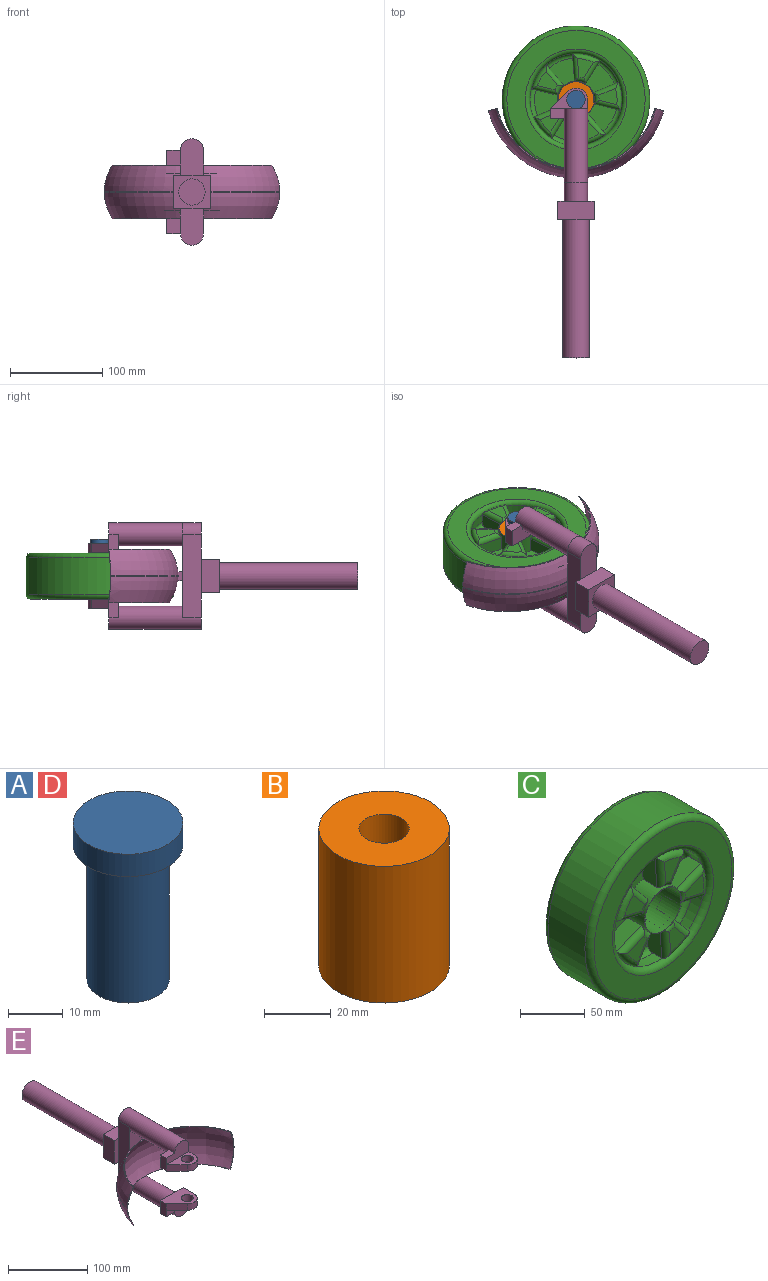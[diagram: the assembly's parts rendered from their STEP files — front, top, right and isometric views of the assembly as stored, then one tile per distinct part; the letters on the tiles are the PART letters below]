
ASSEMBLY  parts=5 mates=4
PART A: 5 faces, bbox 20x20x35 mm
  f0: cylinder r=7.5mm len=30mm, axis (0,0,-1), area 1413.7mm2, adj f3,f4
  f1: cylinder r=10mm len=20mm, axis (0,0,-1), area 314.2mm2, adj f2,f3
  f2: plane 20x20mm, normal (0,0,1), area 314.2mm2, adj f1
  f3: plane 20x20mm, normal (0,0,-1), area 137.4mm2, adj f0,f1
  f4: plane 15x15mm, normal (0,0,-1), area 176.7mm2, adj f0
PART B: 7 faces, bbox 39x39x50 mm
  f0: cylinder r=19.5mm len=50mm, axis (0,0,-1), area 6126.1mm2, adj f1,f2
  f1: plane 39x39mm, normal (0,0,1), area 1017.9mm2, adj f0,f3
  f2: plane 39x39mm, normal (0,0,-1), area 1017.9mm2, adj f0,f5
  f3: cylinder r=7.5mm len=20mm, axis (0,0,1), area 942.5mm2, adj f1,f4
  f4: plane 15x15mm, normal (0,0,1), area 176.7mm2, adj f3
  f5: cylinder r=7.5mm len=20mm, axis (0,0,-1), area 942.5mm2, adj f2,f6
  f6: plane 15x15mm, normal (0,0,-1), area 176.7mm2, adj f5
PART C: 106 faces, bbox 173.2x50x173.2 mm
  f0: plane 27.73x26.51mm, normal (0,-1,0), area 510.5mm2, adj f1,f26,f58,f101
  f1: torus R=45mm, axis (0,-1,0), area 1524.3mm2, adj f0,f4,f6,f8,f10,f15,f25,f26
  f2: plane 27.73x26.51mm, normal (0,1,0), area 510.5mm2, adj f3,f23,f56,f103
  f3: torus R=45mm, axis (0,1,0), area 1524.3mm2, adj f2,f5,f7,f9,f11,f18,f22,f23
  f4: plane 27.96x27.03mm, normal (0,-1,0), area 510.5mm2, adj f1,f50,f59,f101
  f5: plane 27.96x27.03mm, normal (0,1,0), area 510.5mm2, adj f3,f48,f55,f103
  f6: plane 30.77x29.56mm, normal (0,-1,0), area 510.5mm2, adj f1,f42,f51,f101
  f7: plane 30.77x29.56mm, normal (0,1,0), area 510.5mm2, adj f3,f40,f47,f103
  f8: plane 31.13x30.71mm, normal (0,-1,0), area 510.5mm2, adj f1,f34,f43,f101
  f9: plane 31.13x30.71mm, normal (0,1,0), area 510.5mm2, adj f3,f32,f39,f103
  f10: plane 29.64x27.64mm, normal (0,-1,0), area 510.5mm2, adj f1,f25,f35,f101
  f11: plane 29.64x27.64mm, normal (0,1,0), area 510.5mm2, adj f3,f24,f31,f103
  f12: cylinder r=80mm len=160mm, axis (0,1,0), area 20106.2mm2, adj f17,f20
  f13: plane 150x150mm, normal (0,-1,0), area 8168.1mm2, adj f16,f17
  f14: plane 150x150mm, normal (0,1,0), area 8168.1mm2, adj f19,f20
  f15: cylinder r=50mm len=100mm, axis (0,-1,0), area 3141.6mm2, adj f1,f16
  f16: torus R=55mm, axis (0,-1,0), area 2557.1mm2, adj f13,f15
  f17: torus R=75mm, axis (0,-1,0), area 3858.2mm2, adj f12,f13
  f18: cylinder r=50mm len=100mm, axis (0,1,0), area 3141.6mm2, adj f3,f19
  f19: torus R=55mm, axis (0,-1,0), area 2557.1mm2, adj f14,f18
  f20: torus R=75mm, axis (0,-1,0), area 3858.2mm2, adj f12,f14
  f21: plane 22.17x19.85mm, normal (0,1,0), area 230.9mm2, adj f65,f66,f67,f68
  f22: cylinder r=49.55mm len=26.09mm, axis (0,1,0), area 376mm2, adj f3,f23,f24,f65
  f23: plane 28.72x15mm, normal (-0.23,0,-0.97), area 439.5mm2, adj f2,f3,f22,f66,f103
  f24: plane 22.5x19.16mm, normal (0.76,0,0.65), area 439.5mm2, adj f3,f11,f22,f67,f103
  f25: plane 22.5x19.16mm, normal (0.76,0,0.65), area 439.5mm2, adj f1,f10,f27,f87,f101
  f26: plane 28.72x15mm, normal (-0.23,0,-0.97), area 439.5mm2, adj f0,f1,f27,f86,f101
  f27: cylinder r=49.55mm len=26.09mm, axis (0,1,0), area 376mm2, adj f1,f25,f26,f85
  f28: plane 22.17x19.85mm, normal (0,-1,0), area 230.9mm2, adj f85,f86,f87,f88
  f29: plane 21.03x17.35mm, normal (0,1,0), area 230.9mm2, adj f69,f70,f71,f72
  f30: cylinder r=49.55mm len=29.77mm, axis (0,1,0), area 376mm2, adj f3,f31,f32,f69
  f31: plane 29.46x15mm, normal (-1,0,-0.08), area 439.5mm2, adj f3,f11,f30,f70,f103
  f32: plane 25.17x15.47mm, normal (0.85,0,-0.52), area 439.5mm2, adj f3,f9,f30,f71,f103
  f33: cylinder r=49.55mm len=29.77mm, axis (0,1,0), area 376mm2, adj f1,f34,f35,f89
  f34: plane 25.17x15.47mm, normal (0.85,0,-0.52), area 439.5mm2, adj f1,f8,f33,f91,f101
  f35: plane 29.46x15mm, normal (-1,0,-0.08), area 439.5mm2, adj f1,f10,f33,f90,f101
  f36: plane 21.03x17.35mm, normal (0,-1,0), area 230.9mm2, adj f89,f90,f91,f92
  f37: plane 20x17.79mm, normal (0,1,0), area 230.9mm2, adj f73,f74,f75,f76
  f38: cylinder r=49.55mm len=30.53mm, axis (0,1,0), area 376mm2, adj f3,f39,f40,f75
  f39: plane 27.32x15mm, normal (-0.38,0,0.92), area 439.5mm2, adj f3,f9,f38,f76,f103
  f40: plane 28.72x15mm, normal (-0.23,0,-0.97), area 439.5mm2, adj f3,f7,f38,f73,f103
  f41: cylinder r=49.55mm len=30.53mm, axis (0,1,0), area 376mm2, adj f1,f42,f43,f95
  f42: plane 28.72x15mm, normal (-0.23,0,-0.97), area 439.5mm2, adj f1,f6,f41,f93,f101
  f43: plane 27.32x15mm, normal (-0.38,0,0.92), area 439.5mm2, adj f1,f8,f41,f96,f101
  f44: plane 20x17.79mm, normal (0,-1,0), area 230.9mm2, adj f93,f94,f95,f96
  f45: plane 21.86x18.02mm, normal (0,1,0), area 230.9mm2, adj f77,f78,f79,f80
  f46: cylinder r=49.55mm len=28.31mm, axis (0,1,0), area 376mm2, adj f3,f47,f48,f77
  f47: plane 22.5x19.16mm, normal (0.76,0,0.65), area 439.5mm2, adj f3,f7,f46,f78,f103
  f48: plane 29.46x15mm, normal (-1,0,-0.08), area 439.5mm2, adj f3,f5,f46,f79,f103
  f49: cylinder r=49.55mm len=28.31mm, axis (0,1,0), area 376mm2, adj f1,f50,f51,f97
  f50: plane 29.46x15mm, normal (-1,0,-0.08), area 439.5mm2, adj f1,f4,f49,f99,f101
  f51: plane 22.5x19.16mm, normal (0.76,0,0.65), area 439.5mm2, adj f1,f6,f49,f98,f101
  f52: plane 21.86x18.02mm, normal (0,-1,0), area 230.9mm2, adj f97,f98,f99,f100
  f53: plane 21.93x21.13mm, normal (0,1,0), area 230.9mm2, adj f61,f62,f63,f64
  f54: cylinder r=49.55mm len=23.31mm, axis (0,1,0), area 376mm2, adj f3,f55,f56,f61
  f55: plane 25.17x15.47mm, normal (0.85,0,-0.52), area 439.5mm2, adj f3,f5,f54,f62,f103
  f56: plane 27.32x15mm, normal (-0.38,0,0.92), area 439.5mm2, adj f2,f3,f54,f63,f103
  f57: cylinder r=49.55mm len=23.31mm, axis (0,1,0), area 376mm2, adj f1,f58,f59,f81
  f58: plane 27.32x15mm, normal (-0.38,0,0.92), area 439.5mm2, adj f0,f1,f57,f83,f101
  f59: plane 25.17x15.47mm, normal (0.85,0,-0.52), area 439.5mm2, adj f1,f4,f57,f82,f101
  f60: plane 21.93x21.13mm, normal (0,-1,0), area 230.9mm2, adj f81,f82,f83,f84
  f61: torus R=44.55mm, axis (0,1,0), area 207mm2, adj f53,f54,f62,f63
  f62: cylinder r=5mm len=27.79mm, axis (-0.52,0,-0.85), area 204mm2, adj f53,f55,f61,f64
  f63: cylinder r=5mm len=29.22mm, axis (0.92,0,0.38), area 204mm2, adj f53,f56,f61,f64
  f64: torus R=25mm, axis (0,1,0), area 79mm2, adj f53,f62,f63,f103
  f65: torus R=44.55mm, axis (0,1,0), area 207mm2, adj f21,f22,f66,f67
  f66: cylinder r=5mm len=29.9mm, axis (-0.97,0,0.23), area 204mm2, adj f21,f23,f65,f68
  f67: cylinder r=5mm len=25.74mm, axis (0.65,0,-0.76), area 204mm2, adj f21,f24,f65,f68
  f68: torus R=25mm, axis (0,1,0), area 79mm2, adj f21,f66,f67,f103
  f69: torus R=44.55mm, axis (0,1,0), area 207mm2, adj f29,f30,f70,f71
  f70: cylinder r=5mm len=29.85mm, axis (-0.08,0,1), area 204mm2, adj f29,f31,f69,f72
  f71: cylinder r=5mm len=27.79mm, axis (-0.52,0,-0.85), area 204mm2, adj f29,f32,f69,f72
  f72: torus R=25mm, axis (0,1,0), area 79mm2, adj f29,f70,f71,f103
  f73: cylinder r=5mm len=29.9mm, axis (-0.97,0,0.23), area 204mm2, adj f37,f40,f74,f75
  f74: torus R=25mm, axis (0,1,0), area 79mm2, adj f37,f73,f76,f103
  f75: torus R=44.55mm, axis (0,1,0), area 207mm2, adj f37,f38,f73,f76
  f76: cylinder r=5mm len=29.22mm, axis (0.92,0,0.38), area 204mm2, adj f37,f39,f74,f75
  f77: torus R=44.55mm, axis (0,1,0), area 207mm2, adj f45,f46,f78,f79
  f78: cylinder r=5mm len=25.74mm, axis (0.65,0,-0.76), area 204mm2, adj f45,f47,f77,f80
  f79: cylinder r=5mm len=29.85mm, axis (-0.08,0,1), area 204mm2, adj f45,f48,f77,f80
  f80: torus R=25mm, axis (0,1,0), area 79mm2, adj f45,f78,f79,f103
  f81: torus R=44.55mm, axis (0,1,0), area 207mm2, adj f57,f60,f82,f83
  f82: cylinder r=5mm len=27.79mm, axis (0.52,0,0.85), area 204mm2, adj f59,f60,f81,f84
  f83: cylinder r=5mm len=29.22mm, axis (-0.92,0,-0.38), area 204mm2, adj f58,f60,f81,f84
  f84: torus R=25mm, axis (0,1,0), area 79mm2, adj f60,f82,f83,f101
  f85: torus R=44.55mm, axis (0,1,0), area 207mm2, adj f27,f28,f86,f87
  f86: cylinder r=5mm len=29.9mm, axis (0.97,0,-0.23), area 204mm2, adj f26,f28,f85,f88
  f87: cylinder r=5mm len=25.74mm, axis (-0.65,0,0.76), area 204mm2, adj f25,f28,f85,f88
  f88: torus R=25mm, axis (0,1,0), area 79mm2, adj f28,f86,f87,f101
  f89: torus R=44.55mm, axis (0,1,0), area 207mm2, adj f33,f36,f90,f91
  f90: cylinder r=5mm len=29.85mm, axis (0.08,0,-1), area 204mm2, adj f35,f36,f89,f92
  f91: cylinder r=5mm len=27.79mm, axis (0.52,0,0.85), area 204mm2, adj f34,f36,f89,f92
  f92: torus R=25mm, axis (0,1,0), area 79mm2, adj f36,f90,f91,f101
  f93: cylinder r=5mm len=29.9mm, axis (0.97,0,-0.23), area 204mm2, adj f42,f44,f94,f95
  f94: torus R=25mm, axis (0,1,0), area 79mm2, adj f44,f93,f96,f101
  f95: torus R=44.55mm, axis (0,1,0), area 207mm2, adj f41,f44,f93,f96
  f96: cylinder r=5mm len=29.22mm, axis (-0.92,0,-0.38), area 204mm2, adj f43,f44,f94,f95
  f97: torus R=44.55mm, axis (0,1,0), area 207mm2, adj f49,f52,f98,f99
  f98: cylinder r=5mm len=25.74mm, axis (-0.65,0,0.76), area 204mm2, adj f51,f52,f97,f100
  f99: cylinder r=5mm len=29.85mm, axis (0.08,0,-1), area 204mm2, adj f50,f52,f97,f100
  f100: torus R=25mm, axis (0,1,0), area 79mm2, adj f52,f98,f99,f101
  f101: cylinder r=20mm len=40mm, axis (0,1,0), area 1570.8mm2, adj f0,f4,f6,f8,f10,f25,f26,f34
  f102: cylinder r=19.5mm len=50mm, axis (0,1,0), area 6126.1mm2, adj f104,f105
  f103: cylinder r=20mm len=40mm, axis (0,1,0), area 1570.8mm2, adj f2,f5,f7,f9,f11,f23,f24,f31
  f104: plane 40x40mm, normal (0,-1,0), area 62mm2, adj f101,f102
  f105: plane 40x40mm, normal (0,1,0), area 62mm2, adj f102,f103
PART D: same geometry as A
PART E: 55 faces, bbox 191.4x292.5x115.4 mm
  f0: plane 39.52x25mm, normal (0,1,0), area 920.9mm2, adj f2,f5,f6,f30
  f1: plane 90x25mm, normal (0,-1,0), area 1667.7mm2, adj f5,f6,f17,f18,f38,f40,f41,f42
  f2: cylinder r=12.5mm len=25mm, axis (0,1,0), area 799.9mm2, adj f0,f3,f5,f6,f18
  f3: plane 25x12.51mm, normal (0,-1,0), area 0.5mm2, adj f2,f18
  f4: plane 39.5x25mm, normal (0,1,0), area 920.4mm2, adj f5,f6,f17,f32
  f5: plane 90.01x20.01mm, normal (-1,0,0), area 1800mm2, adj f0,f1,f2,f4,f17,f29
  f6: plane 90.01x20.01mm, normal (1,0,0), area 1800mm2, adj f0,f1,f2,f4,f17,f35
  f7: plane 15x10mm, normal (0,0,1), area 150mm2, adj f11,f12,f16,f17
  f8: plane 18.66x18.66mm, normal (-0.71,-0.71,0), area 263.9mm2, adj f9,f12,f14,f15
  f9: cylinder r=12.5mm len=21.34mm, axis (0,0,-1), area 294.5mm2, adj f8,f10,f14,f15
  f10: plane 20x20mm, normal (1,0,0), area 300mm2, adj f9,f11,f14,f15,f16,f17
  f11: plane 40x20mm, normal (0,1,0), area 554.6mm2, adj f7,f10,f12,f15,f17
  f12: plane 20x10.18mm, normal (-1,0,0), area 201.8mm2, adj f7,f8,f11,f14,f15,f16
  f13: cylinder r=7.5mm len=15mm, axis (0,0,-1), area 471.2mm2, adj f14,f15
  f14: plane 40x22.5mm, normal (0,0,1), area 437.2mm2, adj f8,f9,f10,f12,f13,f16
  f15: plane 40x32.5mm, normal (0,0,-1), area 837.2mm2, adj f8,f9,f10,f11,f12,f13
  f16: plane 40x22.5mm, normal (0,-1,0), area 645.4mm2, adj f7,f10,f12,f14,f17
  f17: cylinder r=12.5mm len=100mm, axis (0,-1,0), area 6675.9mm2, adj f1,f4,f5,f6,f7,f10,f11,f16
  f18: cylinder r=12.5mm len=80mm, axis (0,1,0), area 5890.5mm2, adj f1,f2,f3,f19,f22,f23,f24
  f19: plane 20x20mm, normal (1,0,0), area 300mm2, adj f18,f20,f23,f24,f26,f28
  f20: plane 40x32.5mm, normal (0,0,1), area 835.6mm2, adj f19,f21,f24,f25,f26,f27
  f21: plane 20x10mm, normal (-1,0,0), area 200mm2, adj f20,f22,f23,f24,f25
  f22: plane 15x10mm, normal (0,0,-1), area 150mm2, adj f18,f21,f23,f24
  f23: plane 40x22.5mm, normal (0,-1,0), area 645.4mm2, adj f18,f19,f21,f22,f28
  f24: plane 40x20mm, normal (0,1,0), area 554.6mm2, adj f18,f19,f20,f21,f22
  f25: plane 18.8x18.62mm, normal (-0.71,-0.7,0), area 264.6mm2, adj f20,f21,f26,f28
  f26: cylinder r=12.5mm len=21.38mm, axis (0,0,1), area 295.1mm2, adj f19,f20,f25,f28
  f27: cylinder r=7.5mm len=15mm, axis (0,0,1), area 471.2mm2, adj f20,f28
  f28: plane 40x22.5mm, normal (0,0,-1), area 435.6mm2, adj f19,f23,f25,f26,f27
  f29: plane 36.34x7.5mm, normal (0,-1,0), area 272.6mm2, adj f5,f30,f31,f32
  f30: plane 40x20mm, normal (0,0,-1), area 800mm2, adj f0,f29,f31,f33,f34,f35
  f31: plane 36.34x20mm, normal (-1,0,0), area 726.8mm2, adj f29,f30,f32,f34
  f32: plane 40x20mm, normal (0,0,1), area 800mm2, adj f4,f29,f31,f33,f34,f35
  f33: plane 36.34x20mm, normal (1,0,0), area 726.8mm2, adj f30,f32,f34,f35
  f34: plane 40x36.34mm, normal (0,1,0), area 819mm2, adj f30,f31,f32,f33,f36
  f35: plane 36.34x7.5mm, normal (0,-1,0), area 272.6mm2, adj f6,f30,f32,f33
  f36: cylinder r=14.21mm len=150mm, axis (0,-1,0), area 13396.4mm2, adj f34,f37
  f37: plane 28.43x28.43mm, normal (0,1,0), area 634.7mm2, adj f36
  f38: plane 10x5.39mm, normal (0,0,1), area 53mm2, adj f1,f41,f42,f48
  f39: extruded ~10x0.61mm, area 6.1mm2, adj f41,f42,f51,f52,f53,f54
  f40: plane 10x5.34mm, normal (0,0,-1), area 52.5mm2, adj f1,f41,f42,f46
  f41: plane 10.02x5.41mm, normal (1,0,0), area 52mm2, adj f1,f38,f39,f40,f46,f48,f51,f53
  f42: plane 10.02x5.41mm, normal (-1,0,0), area 52mm2, adj f1,f38,f39,f40,f46,f48,f52,f54
  f43: plane 173.16x66.74mm, normal (0,0,1), area 272.8mm2, adj f44,f48,f49,f50
  f44: revolved ~188.32x74.59mm, area 15209.8mm2, adj f43,f45,f49,f50
  f45: plane 173.33x66.81mm, normal (0,0,-1), area 273.6mm2, adj f44,f46,f49,f50
  f46: revolved ~190.25x75.26mm, area 7477mm2, adj f40,f41,f42,f45,f47,f49,f50
  f47: cylinder r=98.48mm len=190.25mm, axis (0,0,-1), area 158mm2, adj f46,f48,f49,f50,f51,f52,f53,f54
  f48: revolved ~190.25x75.28mm, area 7621.9mm2, adj f38,f41,f42,f43,f47,f49,f50
  f49: plane 59.07x10.26mm, normal (-0.26,-0.97,0), area 61.5mm2, adj f43,f44,f45,f46,f47,f48
  f50: plane 59.07x10.26mm, normal (0.26,-0.97,0), area 61.5mm2, adj f43,f44,f45,f46,f47,f48
  f51: plane 5x0.13mm, normal (0,0,-1), area 0.2mm2, adj f39,f41,f47
  f52: plane 5x0.13mm, normal (0,0,-1), area 0.2mm2, adj f39,f42,f47
  f53: plane 5x0.13mm, normal (0,0,1), area 0.2mm2, adj f39,f41,f47
  f54: plane 5x0.13mm, normal (0,0,1), area 0.2mm2, adj f39,f42,f47
PLACE A t=(-286.71,-376.07,-262.27)mm
PLACE B t=(-286.71,-376.07,-292.27)mm
PLACE C rot(axis=(-1,0,0),90deg) t=(-286.71,-376.07,-292.27)mm
PLACE D rot(axis=(0,1,0),180deg) t=(-286.71,-376.07,-257.27)mm
PLACE E rot(axis=(-1,0,0),180deg) t=(-286.71,-376.07,-292.27)mm fixed
MATE fastened B.f3 <-> E.f9  axis (0,0,-1) through (-286.71,-376.07,-292.27)mm
MATE revolute C.f12 <-> D.f1  axis (0,0,-1) through (-286.71,-376.07,-292.27)mm
MATE revolute B.f0 <-> C.f1  axis (0,0,1) through (-286.71,-376.07,-242.27)mm
MATE slider A.f0 <-> B.f3  axis (0,0,-1) through (-286.71,-376.07,-247.27)mm
